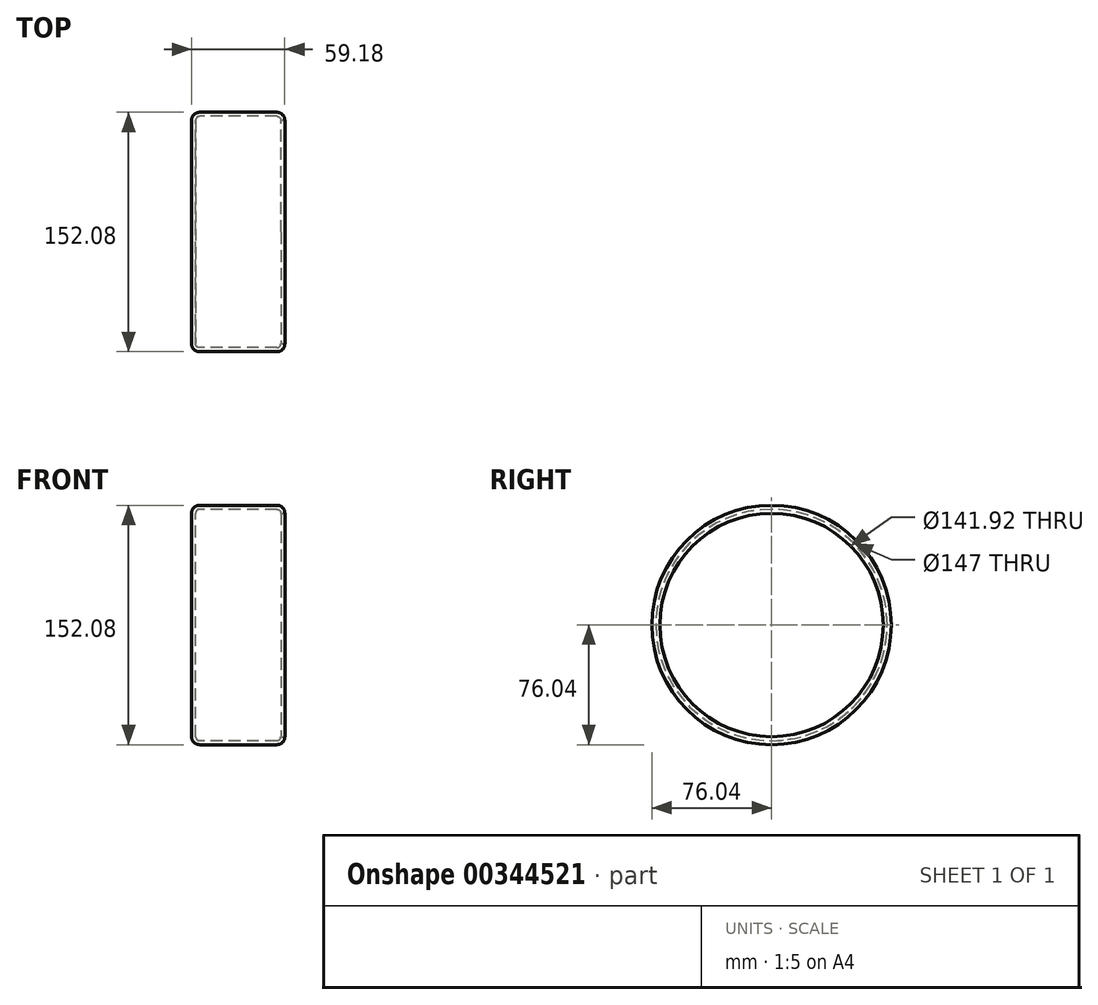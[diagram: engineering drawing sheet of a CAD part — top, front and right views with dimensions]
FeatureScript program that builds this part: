
annotation { "Feature Type Name" : "Feature", "Feature Type Description" : "" }
export const myFeature = defineFeature(function(context is Context, id is Id, definition is map)
    precondition{}
    {
        {
            var Q0;
            Q0=qCreatedBy(makeId("Right.planeOp"),FACE);
            var sketch = newSketch(context, id + "F0", { "sketchPlane" : qUnion([Q0])});
            skCircle(sketch, "E0", {"center": v(0, 0) * mm, "radius": 76.04 * mm});
            skSolve(sketch);
        }
        {
            var Q0;
            Q0=makeQuery(id+"F0.imprint","IMPRINT",FACE,{"disambiguationData":[TD([[makeQuery(id+"F0.imprint","IMPRINT",EDGE,{"derivedFrom":sQuery(id+"F0.wireOp",EDGE,"E0")}),1.0]])]});
            extrude(context, id + "F1", {"entities" : qUnion([Q0]), "depth" : 59.18 * mm});
        }
        {
            var Q0;
            Q0=makeQuery(id+"F1.opExtrude","CAP_EDGE",EDGE,{"disambiguationData":[OSD([sQuery(id+"F0.wireOp",EDGE,"E0")])],"isStart":false});
            fillet(context, id + "F2", {"entities" : qUnion([Q0]), "radius" : 5.08 * mm, "tangentPropagation" : true, "allowEdgeOverflow" : false});
        }
        {
            var Q0;
            Q0=makeQuery(id+"F1.opExtrude","CAP_EDGE",EDGE,{"disambiguationData":[OSD([sQuery(id+"F0.wireOp",EDGE,"E0")])],"isStart":true});
            fillet(context, id + "F3", {"entities" : qUnion([Q0]), "radius" : 5.08 * mm, "tangentPropagation" : true, "allowEdgeOverflow" : false});
        }
        {
            var Q0;
            Q0=makeQuery(id+"F1.opExtrude","CAP_FACE",FACE,{"disambiguationData":[OSD([sQuery(id+"F0.wireOp",EDGE,"E0")])],"isStart":false});
            shell(context, id + "F4", {"entities" : qUnion([Q0]), "thickness" : 2.54 * mm});
        }
    });
